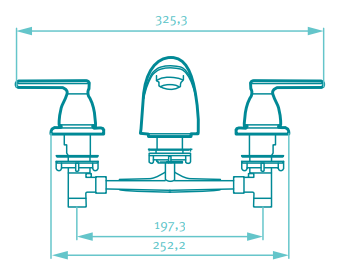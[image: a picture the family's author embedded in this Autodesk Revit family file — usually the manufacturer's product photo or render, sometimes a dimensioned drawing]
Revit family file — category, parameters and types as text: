
# Revit family: 54115551_Lavamanos_8In_Nogal
name_source: partatom
category: Plumbing Fixtures
units: mm (PartAtom-declared; Revit-internal decimal feet)

## family parameters
Cut with Voids When Loaded = No
Host = Face
OmniClass Number = 23.31.11.00
OmniClass Title = Faucets
Part Type = Normal
Room Calculation Point = No
Round Connector Dimension = Use Diameter
Shared = No

## types (1)
- 54115551_Lavamanos_8In_Nogal
    Alto = 171 mm
    Ancho = 325 mm
    Capacidad de flujo = A 60 psi: 8.3 L/min.
    Ciclo de vida de la unidad de cierre = 500000 ciclos.
    Creado por = BIMBAU
    Default Elevation = 0 mm  [stored 0 ft]
    Description = El lavamanos 8 Pulgadas Nogal ha sido diseñada para trabajar en perfecta armonía con el espacio; Inspirada en las necesidades del consumidor latinoamericano dando como resultado un producto robusto y funcional. Permite regular la temperatura del agua por medio de dos manijas independientes. Incorpora un sistema aireador que genera un chorro de agua espumoso, agradable al tacto.
    Dimensiones generales del producto = 94 x 325.3 x 167 mm.
    Diámetro abasto = 13 mm
    Fecha de creación = 13/04/2021
    Garantía = 30 años Grival - 5 años Cromado.
    Manufacturer = Corona.
    Material = Corona_Cromado
    Material 2 = Corona_Acero inoxidable
    Model = 54115551_Lavamanos_8In_Nogal
    Normatividad = NTC 1644.
    Peso Bruto aprox = 960 gr. / 2.12 lb.
    Peso Neto aprox = 850 gr. / 1.87 lb.
    Presión máxima recomendada = 125 psi.
    Presión mínima recomendada = 20 psi.
    Profundidad = 167 mm
    Recubrimientos = Resistente a la corrosión, pelado y decoloración por agua. Recubrimientos no tóxicos. Producto para uso doméstico.
    Referencia = 54115551
    Temperaturas máxima de trabajo = 71° C / 159.8° F.
    Temperaturas mínima de trabajo = 5° C/ 41° F.

note: [stored X ft] marks values corroborated as IEEE doubles in the binary element streams (Revit-internal decimal feet)

## geometry (parser evidence)
native form markers: Sweep x4
no freeform markers — native parametric forms only
